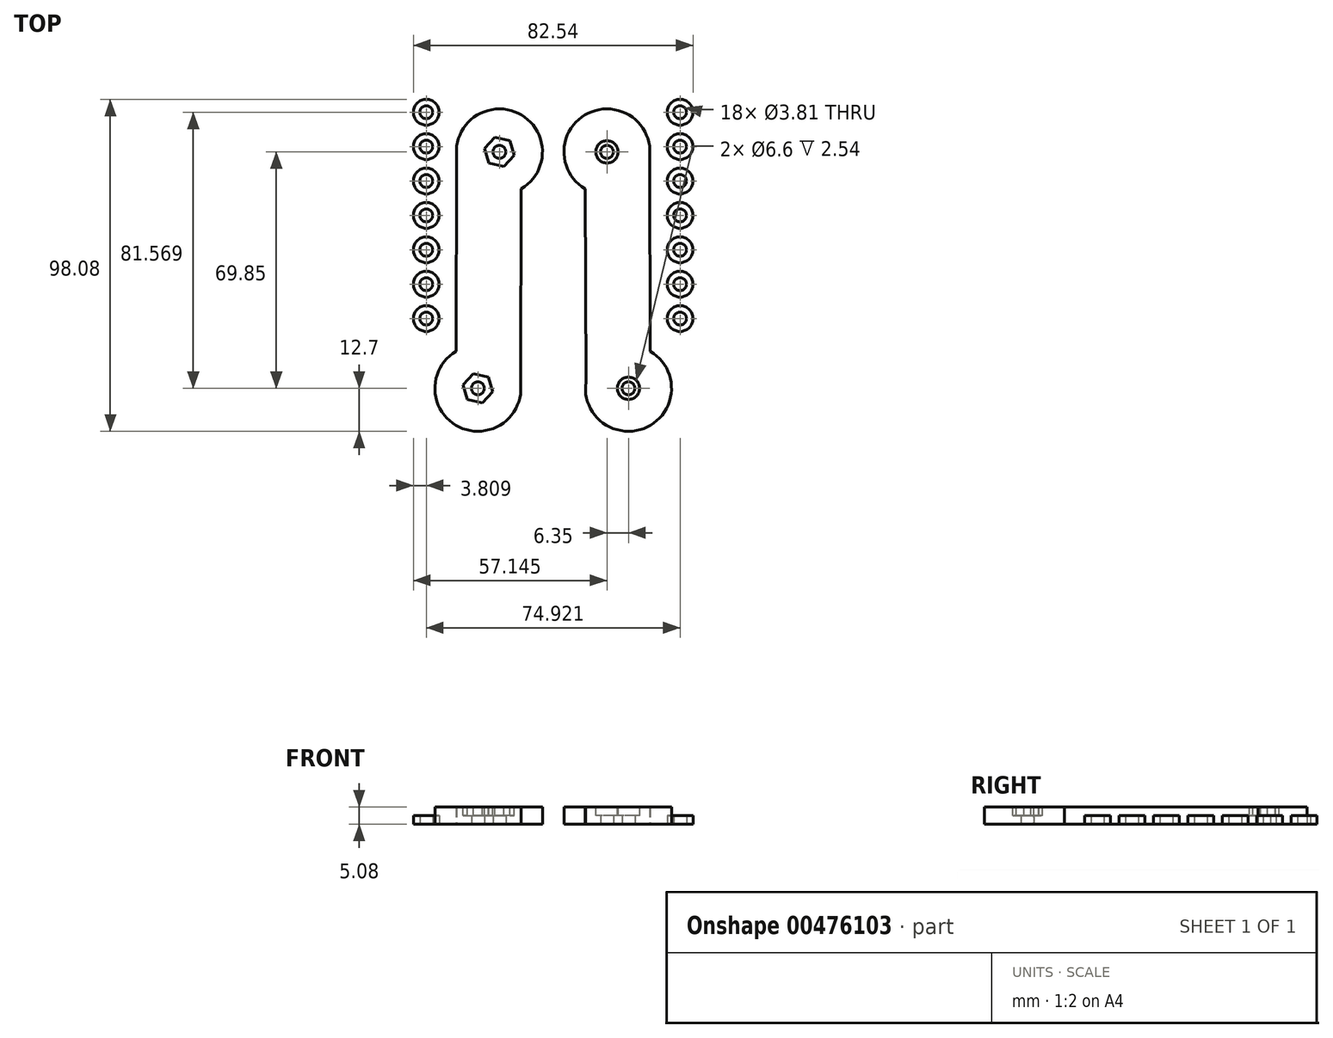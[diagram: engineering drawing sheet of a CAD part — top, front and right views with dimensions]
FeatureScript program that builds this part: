
annotation { "Feature Type Name" : "Feature", "Feature Type Description" : "" }
export const myFeature = defineFeature(function(context is Context, id is Id, definition is map)
    precondition{}
    {
        {
            var Q0;
            Q0=qCreatedBy(makeId("Top.planeOp"),FACE);
            var sketch = newSketch(context, id + "F0", { "sketchPlane" : qUnion([Q0])});
            skCircle(sketch, "E0", {"center": v(-15.88, 31.75) * mm, "radius": 1.9 * mm});
            skCircle(sketch, "E1", {"center": v(-22.22, -38.1) * mm, "radius": 1.9 * mm});
            skCircle(sketch, "E2", {"center": v(-22.22, -38.1) * mm, "radius": 12.7 * mm});
            skCircle(sketch, "E3", {"center": v(-15.88, 31.75) * mm, "radius": 12.7 * mm});
            skLineSegment(sketch, "E4", {"start": v(-28.45, 30) * mm, "end": v(-28.66, -27.15) * mm});
            skLineSegment(sketch, "E5", {"start": v(-9.65, -36.35) * mm, "end": v(-9.44, 20.8) * mm});
            skCircle(sketch, "E6.MirrorC", {"center": v(15.88, 31.75) * mm, "radius": 1.9 * mm});
            skCircle(sketch, "E7.MirrorC", {"center": v(22.22, -38.1) * mm, "radius": 1.9 * mm});
            skCircle(sketch, "E8.MirrorC", {"center": v(22.22, -38.1) * mm, "radius": 12.7 * mm});
            skLineSegment(sketch, "E9.MirrorCS", {"start": v(28.45, 30) * mm, "end": v(28.66, -27.15) * mm});
            skCircle(sketch, "E10.MirrorC", {"center": v(15.88, 31.75) * mm, "radius": 12.7 * mm});
            skLineSegment(sketch, "E11.MirrorCS", {"start": v(9.65, -36.35) * mm, "end": v(9.44, 20.8) * mm});
            skSolve(sketch);
        }
        {
            var Q0;
            Q0 = qSketchRegion(id + "F0", true);
            extrude(context, id + "F1", {"entities" : qUnion([Q0]), "depth" : 5.08 * mm});
        }
        {
            var Q0;
            Q0=makeQuery(id+"F1.opExtrude","CAP_FACE",FACE,{"disambiguationData":[OSD([sQuery(id+"F0.wireOp",EDGE,"E0"),sQuery(id+"F0.wireOp",EDGE,"E1"),sQuery(id+"F0.wireOp",EDGE,"E2"),sQuery(id+"F0.wireOp",EDGE,"E3"),sQuery(id+"F0.wireOp",EDGE,"E4"),sQuery(id+"F0.wireOp",EDGE,"E5")])],"isStart":false});
            var sketch = newSketch(context, id + "F2", { "sketchPlane" : qUnion([Q0])});
            skCircle(sketch, "E12.cCircle", {"center": v(-15.88, 31.75) * mm, "radius": 3.94 * mm, "construction": true});
            skLineSegment(sketch, "E12.0", {"start": v(-11.44, 30.75) * mm, "end": v(-14.52, 27.41) * mm});
            skLineSegment(sketch, "E12.1", {"start": v(-14.52, 27.41) * mm, "end": v(-18.96, 28.4) * mm});
            skLineSegment(sketch, "E12.2", {"start": v(-18.96, 28.4) * mm, "end": v(-20.31, 32.75) * mm});
            skLineSegment(sketch, "E12.3", {"start": v(-20.31, 32.75) * mm, "end": v(-17.23, 36.09) * mm});
            skLineSegment(sketch, "E12.4", {"start": v(-17.23, 36.09) * mm, "end": v(-12.8, 35.1) * mm});
            skLineSegment(sketch, "E12.5", {"start": v(-12.8, 35.1) * mm, "end": v(-11.44, 30.75) * mm});
            skPoint(sketch, "E12.0.midPoint", {"position": v(-12.98, 29.08) * mm});
            skCircle(sketch, "E13.cCircle", {"center": v(-22.22, -38.1) * mm, "radius": 3.94 * mm, "construction": true});
            skLineSegment(sketch, "E13.0", {"start": v(-17.79, -39.1) * mm, "end": v(-20.87, -42.44) * mm});
            skLineSegment(sketch, "E13.1", {"start": v(-20.87, -42.44) * mm, "end": v(-25.3, -41.44) * mm});
            skLineSegment(sketch, "E13.2", {"start": v(-25.3, -41.44) * mm, "end": v(-26.66, -37.1) * mm});
            skLineSegment(sketch, "E13.3", {"start": v(-26.66, -37.1) * mm, "end": v(-23.58, -33.76) * mm});
            skLineSegment(sketch, "E13.4", {"start": v(-23.58, -33.76) * mm, "end": v(-19.14, -34.76) * mm});
            skLineSegment(sketch, "E13.5", {"start": v(-19.14, -34.76) * mm, "end": v(-17.79, -39.1) * mm});
            skPoint(sketch, "E13.0.midPoint", {"position": v(-19.33, -40.77) * mm});
            skSolve(sketch);
        }
        {
            var Q0;
            Q0 = qSketchRegion(id + "F2", true);
            extrude(context, id + "F3", {"entities" : qUnion([Q0]), "operationType" : NewBodyOperationType.REMOVE, "oppositeDirection" : true, "depth" : 2.54 * mm});
        }
        {
            var Q0;
            Q0=makeQuery(id+"F1.opExtrude","CAP_FACE",FACE,{"disambiguationData":[OSD([sQuery(id+"F0.wireOp",EDGE,"E6.MirrorC"),sQuery(id+"F0.wireOp",EDGE,"E7.MirrorC"),sQuery(id+"F0.wireOp",EDGE,"E8.MirrorC"),sQuery(id+"F0.wireOp",EDGE,"E9.MirrorCS"),sQuery(id+"F0.wireOp",EDGE,"E10.MirrorC"),sQuery(id+"F0.wireOp",EDGE,"E11.MirrorCS")])],"isStart":false});
            var sketch = newSketch(context, id + "F4", { "sketchPlane" : qUnion([Q0])});
            skCircle(sketch, "E14", {"center": v(15.88, 31.75) * mm, "radius": 3.3 * mm});
            skCircle(sketch, "E15", {"center": v(22.22, -38.1) * mm, "radius": 3.3 * mm});
            skSolve(sketch);
        }
        {
            var Q0;
            Q0 = qSketchRegion(id + "F4", true);
            extrude(context, id + "F5", {"entities" : qUnion([Q0]), "operationType" : NewBodyOperationType.REMOVE, "oppositeDirection" : true, "depth" : 2.54 * mm});
        }
        {
            var Q0;
            Q0=qCreatedBy(makeId("Top.planeOp"),FACE);
            var sketch = newSketch(context, id + "F6", { "sketchPlane" : qUnion([Q0])});
            skCircle(sketch, "E16", {"center": v(37.46, 33.3) * mm, "radius": 1.9 * mm});
            skCircle(sketch, "E17", {"center": v(37.46, 23.15) * mm, "radius": 1.9 * mm});
            skCircle(sketch, "E18", {"center": v(37.46, 12.99) * mm, "radius": 1.9 * mm});
            skCircle(sketch, "E19", {"center": v(37.46, 43.47) * mm, "radius": 1.9 * mm});
            skCircle(sketch, "E20", {"center": v(37.46, 2.83) * mm, "radius": 1.9 * mm});
            skCircle(sketch, "E21", {"center": v(37.46, -7.33) * mm, "radius": 1.9 * mm});
            skCircle(sketch, "E22", {"center": v(37.46, -17.5) * mm, "radius": 1.9 * mm});
            skCircle(sketch, "E23", {"center": v(37.46, 43.47) * mm, "radius": 3.81 * mm});
            skCircle(sketch, "E24", {"center": v(37.46, 33.3) * mm, "radius": 3.81 * mm});
            skCircle(sketch, "E25", {"center": v(37.46, 23.15) * mm, "radius": 3.81 * mm});
            skCircle(sketch, "E26", {"center": v(37.46, 12.99) * mm, "radius": 3.81 * mm});
            skCircle(sketch, "E27", {"center": v(37.46, 2.83) * mm, "radius": 3.81 * mm});
            skCircle(sketch, "E28", {"center": v(37.46, -7.33) * mm, "radius": 3.81 * mm});
            skCircle(sketch, "E29", {"center": v(37.46, -17.5) * mm, "radius": 3.81 * mm});
            skCircle(sketch, "E30.MirrorC", {"center": v(-37.46, 12.99) * mm, "radius": 1.9 * mm});
            skCircle(sketch, "E31.MirrorC", {"center": v(-37.46, 23.15) * mm, "radius": 1.9 * mm});
            skCircle(sketch, "E32.MirrorC", {"center": v(-37.46, 43.47) * mm, "radius": 1.9 * mm});
            skCircle(sketch, "E33.MirrorC", {"center": v(-37.46, 33.3) * mm, "radius": 1.9 * mm});
            skCircle(sketch, "E34.MirrorC", {"center": v(-37.46, 2.83) * mm, "radius": 1.9 * mm});
            skCircle(sketch, "E35.MirrorC", {"center": v(-37.46, -17.5) * mm, "radius": 3.81 * mm});
            skCircle(sketch, "E36.MirrorC", {"center": v(-37.46, -7.33) * mm, "radius": 1.9 * mm});
            skCircle(sketch, "E37.MirrorC", {"center": v(-37.46, -17.5) * mm, "radius": 1.9 * mm});
            skCircle(sketch, "E38.MirrorC", {"center": v(-37.46, 43.47) * mm, "radius": 3.81 * mm});
            skCircle(sketch, "E39.MirrorC", {"center": v(-37.46, -7.33) * mm, "radius": 3.81 * mm});
            skCircle(sketch, "E40.MirrorC", {"center": v(-37.46, 2.83) * mm, "radius": 3.81 * mm});
            skCircle(sketch, "E41.MirrorC", {"center": v(-37.46, 33.3) * mm, "radius": 3.81 * mm});
            skCircle(sketch, "E42.MirrorC", {"center": v(-37.46, 23.15) * mm, "radius": 3.81 * mm});
            skCircle(sketch, "E43.MirrorC", {"center": v(-37.46, 12.99) * mm, "radius": 3.81 * mm});
            skSolve(sketch);
        }
        {
            var Q0;
            Q0 = qSketchRegion(id + "F6", true);
            extrude(context, id + "F7", {"entities" : qUnion([Q0]), "depth" : 2.54 * mm});
        }
    });
